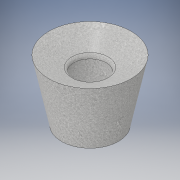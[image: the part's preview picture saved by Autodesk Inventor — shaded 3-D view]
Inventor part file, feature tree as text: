
AUTODESK INVENTOR PART (.ipt)
format: ipt  version: 2017 SP1 (Build 210196100, 196)  size: 168,960 bytes
history: native  units: in
note: dims shown in document units (in); Inventor stores cm internally (conversion verified against a paired STEP export)
features: revolve x1, sketch x1
ambient origin geometry x8: Origin, YZ Plane, XZ Plane, XY Plane, X Axis, Y Axis, Z Axis, Center Point
bodies: Body1 (feature_tree)
feature tree (2):
  revolve  "Revolution3"  [1 undecoded]
  sketch  "Sketch1"  dims[d0=1.13in d3=0.1718in d5=1.0in d6=1.0in d7=90.0deg d8=0.5in d9=15.0deg d31=0.25in d34=15.0deg d37=1.75in d40=3.75in d41=0.125in d46=0.75in d47=0.5in d51=0.5in d52=0.25in d54=0.5in d55=0.5in d56=1.25in d58=0.0017in d59=0.5in d60=0.5in d61=1.0in d62=0.234in d63=0.234in d64=0.125in d67=0.25in d68=4.25in d69=0.25in d70=0.25in d71=0.125in d73=3.4in d74=1.25in d75=0.2498in d77=90.0deg]
note: 1 required parameter value undecoded (feature->parameter linkage not recoverable at this tier; creation-order binding heuristic only, values carry confidence <= 0.55)
